FCSTD DOCUMENT  (FreeCAD 0.19R24276 (Git))
Label: Master_sketch
License: All rights reserved
LicenseURL: http://en.wikipedia.org/wiki/All_rights_reserved
objects: Sketcher::SketchObject×1, PartDesign::Body×1
note: 2 computed .brp shape members not serialized (recipe doc carries the construction recipe); baked Part::Feature solids carry a one-line shape summary decoded from their .brp

FEATURE [Sketcher::SketchObject] Sketch
  FullyConstrained = false
  MapMode = 5
  Support = -> [XY_Plane]
  sketch-geometry (29):
    g0: Circle CenterX=0 CenterY=0 CenterZ=0 NormalX=0 NormalY=0 NormalZ=1 AngleXU=0 Radius=30
    g1: Circle CenterX=0 CenterY=0 CenterZ=0 NormalX=0 NormalY=0 NormalZ=1 AngleXU=0 Radius=35
    g2: Circle CenterX=0 CenterY=0 CenterZ=0 NormalX=0 NormalY=0 NormalZ=1 AngleXU=0 Radius=25
    g3: Circle CenterX=0 CenterY=0 CenterZ=0 NormalX=0 NormalY=0 NormalZ=1 AngleXU=0 Radius=40
    g4: Circle CenterX=0 CenterY=0 CenterZ=0 NormalX=0 NormalY=0 NormalZ=1 AngleXU=0 Radius=32.5
    g5: LineSegment StartX=0 StartY=0 StartZ=0 EndX=32.5 EndY=0 EndZ=0
    g6: LineSegment StartX=0 StartY=0 StartZ=0 EndX=28.1458 EndY=16.25 EndZ=0
    g7: Circle CenterX=28.1458 CenterY=16.25 CenterZ=0 NormalX=0 NormalY=0 NormalZ=1 AngleXU=0 Radius=2.5
    g8: Circle CenterX=32.5 CenterY=0 CenterZ=0 NormalX=0 NormalY=0 NormalZ=1 AngleXU=0 Radius=2.5
    g9: LineSegment StartX=0 StartY=0 StartZ=0 EndX=16.25 EndY=28.1458 EndZ=0
    g10: Circle CenterX=16.25 CenterY=28.1458 CenterZ=0 NormalX=0 NormalY=0 NormalZ=1 AngleXU=0 Radius=2.5
    g11: LineSegment StartX=0 StartY=0 StartZ=0 EndX=0.100138 EndY=32.4998 EndZ=0
    g12: LineSegment StartX=0 StartY=0 StartZ=0 EndX=-16.25 EndY=28.1458 EndZ=0
    g13: LineSegment StartX=0 StartY=0 StartZ=0 EndX=-28.1458 EndY=16.25 EndZ=0
    g14: LineSegment StartX=0 StartY=0 StartZ=0 EndX=-32.5 EndY=-6e-16 EndZ=0
    g15: Circle CenterX=0.100138 CenterY=32.4998 CenterZ=0 NormalX=0 NormalY=0 NormalZ=1 AngleXU=0 Radius=2.5
    g16: Circle CenterX=-28.1458 CenterY=16.25 CenterZ=0 NormalX=0 NormalY=0 NormalZ=1 AngleXU=0 Radius=2.5
    g17: Circle CenterX=-32.5 CenterY=-6e-16 CenterZ=0 NormalX=0 NormalY=0 NormalZ=1 AngleXU=0 Radius=2.5
    g18: Circle CenterX=-16.25 CenterY=28.1458 CenterZ=0 NormalX=0 NormalY=0 NormalZ=1 AngleXU=0 Radius=2.5
    g19: LineSegment StartX=0 StartY=0 StartZ=0 EndX=-28.1458 EndY=-16.25 EndZ=0
    g20: LineSegment StartX=0 StartY=0 StartZ=0 EndX=-16.25 EndY=-28.1458 EndZ=0
    g21: LineSegment StartX=-0.104366 StartY=-3.99902e-07 StartZ=0 EndX=-0.104366 EndY=-32.4998 EndZ=0
    g22: LineSegment StartX=0 StartY=0 StartZ=0 EndX=16.25 EndY=-28.1458 EndZ=0
    g23: LineSegment StartX=0 StartY=0 StartZ=0 EndX=28.1458 EndY=-16.25 EndZ=0
    g24: Circle CenterX=-28.1458 CenterY=-16.25 CenterZ=0 NormalX=0 NormalY=0 NormalZ=1 AngleXU=0 Radius=2.5
    g25: Circle CenterX=-16.25 CenterY=-28.1458 CenterZ=0 NormalX=0 NormalY=0 NormalZ=1 AngleXU=0 Radius=2.5
    g26: Circle CenterX=-0.104366 CenterY=-32.4998 CenterZ=0 NormalX=0 NormalY=0 NormalZ=1 AngleXU=0 Radius=2.5
    g27: Circle CenterX=16.25 CenterY=-28.1458 CenterZ=0 NormalX=0 NormalY=0 NormalZ=1 AngleXU=0 Radius=2.5
    g28: Circle CenterX=28.1458 CenterY=-16.25 CenterZ=0 NormalX=0 NormalY=0 NormalZ=1 AngleXU=0 Radius=2.5
  constraints (68):
    c: Coincident(g0,g-1)
    c: Coincident(g1,g0)
    c: Coincident(g2,g0)
    c: Coincident(g3,g0)
    c: Diameter(g2) = 50
    c: Diameter(g0) = 60
    c: Diameter(g1) = 70
    c: Diameter(g3) = 80
    c: Coincident(g4,g0)
    c: Diameter(g4) = 65
    c: Coincident(g5,g0)
    c: Coincident(g6,g0)
    c: Coincident(g7,g6)
    c: Diameter(g7) = 5
    c: Coincident(g8,g5)
    c: Coincident(g9,g0)
    c: Coincident(g10,g9)
    c: Angle(g5,g6) = 0.523599
    c: Angle(g5,g9) = 1.0472
    c: Coincident(g11,g0)
    c: Coincident(g12,g0)
    c: Coincident(g13,g0)
    c: Coincident(g14,g0)
    c: Angle(g-1,g12) = 2.0944
    c: Angle(g-1,g13) = 2.61799
    c: Angle(g14,g-1) = 3.14159
    c: PointOnObject(g11,g4)
    c: Coincident(g15,g11)
    c: Coincident(g16,g13)
    c: Coincident(g17,g14)
    c: Coincident(g18,g12)
    c: Coincident(g19,g0)
    c: Coincident(g20,g0)
    c: Coincident(g22,g0)
    c: Coincident(g23,g0)
    c: Angle(g23,g-1) = 0.523599
    c: Horizontal(g5)
    c: PointOnObject(g23,g4)
    c: PointOnObject(g22,g4)
    c: PointOnObject(g21,g4)
    c: PointOnObject(g20,g4)
    c: PointOnObject(g19,g4)
    c: Angle(g22,g5) = 1.0472
    c: Perpendicular(g5,g21)
    c: Angle(g20,g21) = 0.523599
    c: Angle(g14,g19) = 0.523599
    c: Coincident(g24,g19)
    c: Coincident(g25,g20)
    c: Coincident(g26,g21)
    c: Coincident(g27,g22)
    c: Coincident(g28,g23)
    c: Diameter(g28) = 5
    c: Equal(g24,g25)
    c: Equal(g25,g26)
    c: Equal(g26,g27)
    c: Equal(g27,g28)
    c: Equal(g11,g12)
    c: Equal(g12,g13)
    c: Equal(g13,g14)
    c: Equal(g9,g6)
    c: Equal(g6,g5)
    c: Equal(g5,g11)
    c: Equal(g8,g7)
    c: Equal(g7,g10)
    c: Equal(g10,g15)
    c: Equal(g17,g16)
    c: Equal(g16,g18)
    c: Equal(g18,g15)
FEATURE [PartDesign::Body] Body
  Group = -> [Sketch]
  Origin = -> Origin
